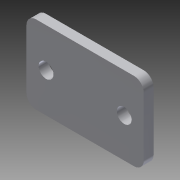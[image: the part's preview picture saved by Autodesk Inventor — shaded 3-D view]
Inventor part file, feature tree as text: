
AUTODESK INVENTOR PART (.ipt)
format: ipt  version: 2014 (Build 180170000, 170)  size: 91,648 bytes
history: native  units: in
note: dims shown in document units (in); Inventor stores cm internally (conversion verified against a paired STEP export)
features: extrude x1, sketch x1
ambient origin geometry x8: Origin, YZ Plane, XZ Plane, XY Plane, X Axis, Y Axis, Z Axis, Center Point
bodies: Solid1 (feature_tree)
feature tree (2):
  extrude  "Extrusion1"  Depth=1.0in
  sketch  "Sketch1"  dims[d0=1.5in d1=1.0in d2=0.19in d3=0.25in d5=0.7874in d7=1.0in d8=0.3937in d10=1.0in d20=0.125in d21=0.125in d22=0.0in]
